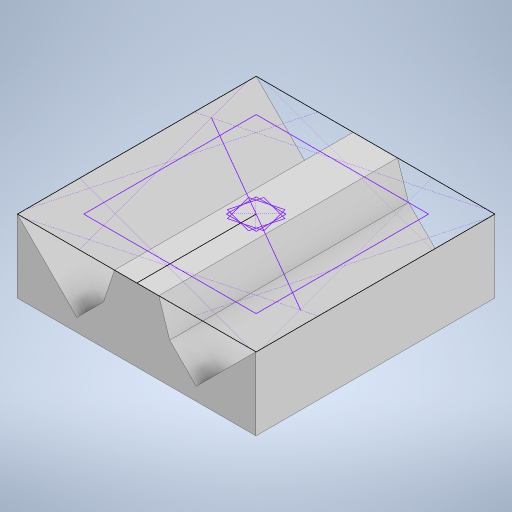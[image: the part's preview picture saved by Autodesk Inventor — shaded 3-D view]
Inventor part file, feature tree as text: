
AUTODESK INVENTOR PART (.ipt)
format: ipt  version: 2023 (Build 270158000, 158)  size: 315,904 bytes
history: native  units: in
note: dims shown in document units (in); Inventor stores cm internally (conversion verified against a paired STEP export)
features: sketch x2, extrude x2
ambient origin geometry x8: Origin, YZ Plane, XZ Plane, XY Plane, X Axis, Y Axis, Z Axis, Center Point
bodies: Solid1 (feature_tree)
feature tree (4):
  sketch  "Sketch1"  dims[d6=36.0in d7=0.0in d18=4.0in]
  extrude  "Extrusion1"  Depth=36.0in
  extrude  "Extrusion2"  Depth=36.0in
  sketch  "Sketch2"  dims[d19=4.0in d20=4.0in d21=4.0in d22=36.0in d23=0.0in d24=0.0in d25=0.0in d26=0.0in d27=0.0in]
